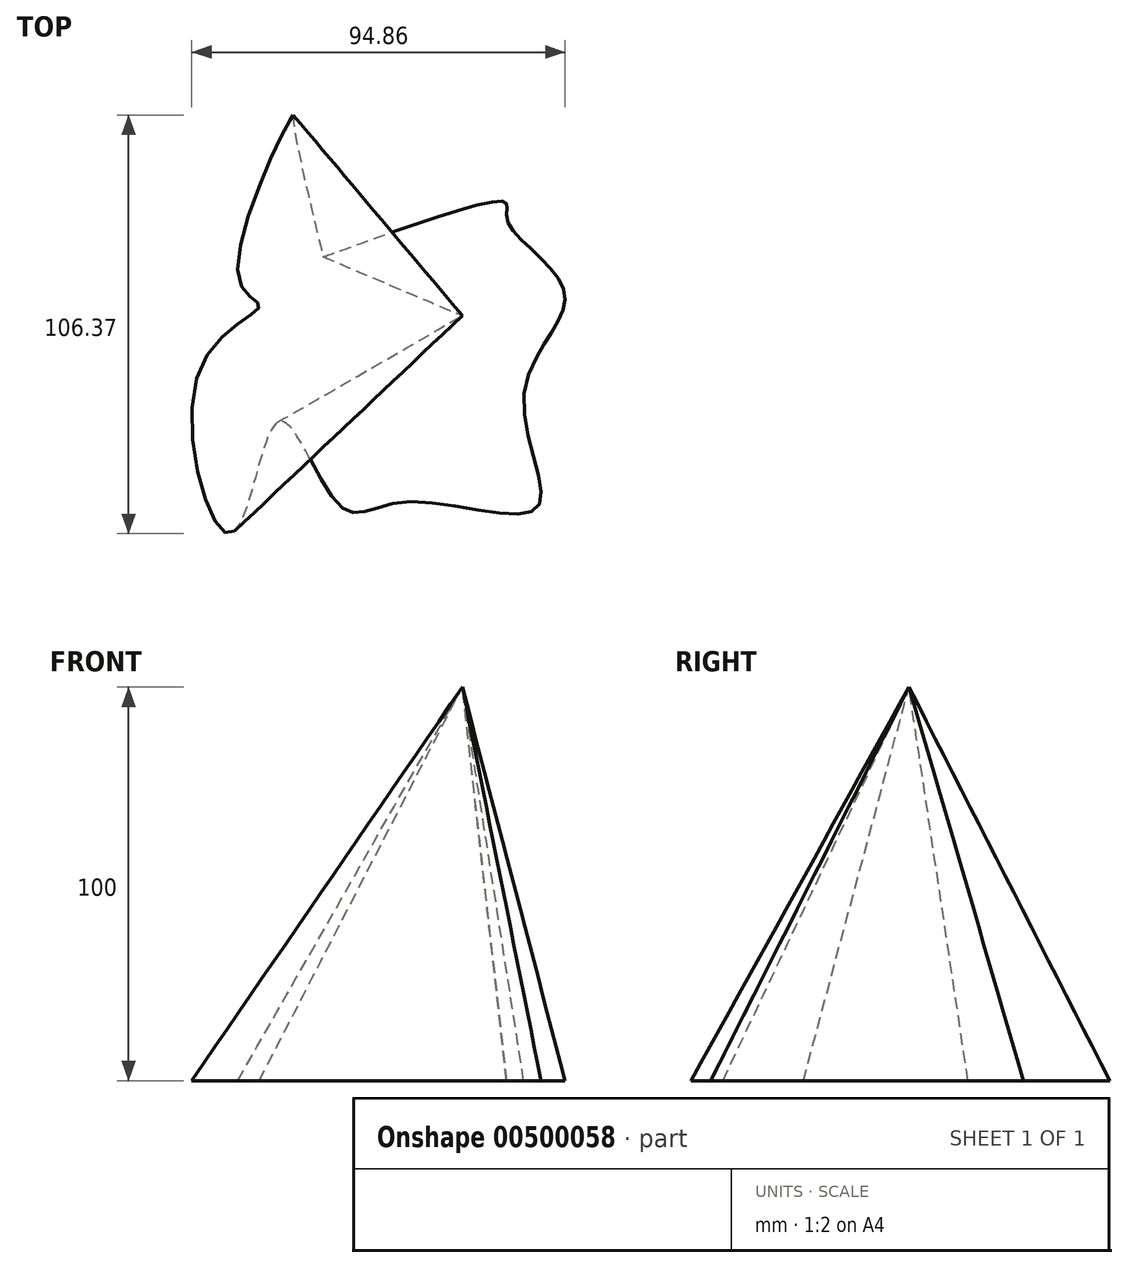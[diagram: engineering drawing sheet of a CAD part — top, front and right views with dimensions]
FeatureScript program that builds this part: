
annotation { "Feature Type Name" : "Feature", "Feature Type Description" : "" }
export const myFeature = defineFeature(function(context is Context, id is Id, definition is map)
    precondition{}
    {
        {
            var Q0;
            Q0=qCreatedBy(makeId("Top.planeOp"),FACE);
            var sketch = newSketch(context, id + "F0", { "sketchPlane" : qUnion([Q0])});
            skFitSpline(sketch, "E0", {"points": [v(-56.84, 9.47) * mm, v(-43.14, 50.86) * mm, v(-42.85, 49.11) * mm, v(-35.56, 15.3) * mm, v(-35.27, 15.01) * mm, v(10.5, 29) * mm, v(11.37, 24.34) * mm, v(25.94, 5.98) * mm, v(15.74, -19.38) * mm, v(18.95, -48.82) * mm, v(-14.87, -47.36) * mm, v(-30.9, -48.53) * mm, v(-46.64, -26.96) * mm, v(-58.59, -55.23) * mm, v(-67.04, -14.43) * mm, v(-51.6, 2.48) * mm, v(-56.84, 9.47) * mm]});
            skSolve(sketch);
        }
        {
            var Q0;
            Q0=qCreatedBy(makeId("Top.planeOp"),FACE);
            cPlane(context, id + "F1", {"entities" : qUnion([Q0]), "cplaneType" : CPlaneType.OFFSET, "offset" : 100 * mm, "width" : 152.4 * mm, "height" : 152.4 * mm});
        }
        {
            var Q0;
            Q0=qCreatedBy(id+"F1.planeOp",FACE);
            var sketch = newSketch(context, id + "F2", { "sketchPlane" : qUnion([Q0])});
            skPoint(sketch, "E1", {"position": v(0, 0) * mm});
            skSolve(sketch);
        }
        {
            var Q0;
            Q0=makeQuery(id+"F0.imprint","IMPRINT",FACE,{"disambiguationData":[TD([[makeQuery(id+"F0.imprint","IMPRINT",EDGE,{"derivedFrom":sQuery(id+"F0.wireOp",EDGE,"E0")}),-1.0]])]});
            var Q1;
            Q1=sQuery(id+"F2.wireOp",VERTEX,"E1");
            loft(context, id + "F3", {"sheetProfilesArray" : [{ "sheetProfileEntities" : qUnion([Q0]) }, { "sheetProfileEntities" : qUnion([Q1]) }]});
        }
    });
